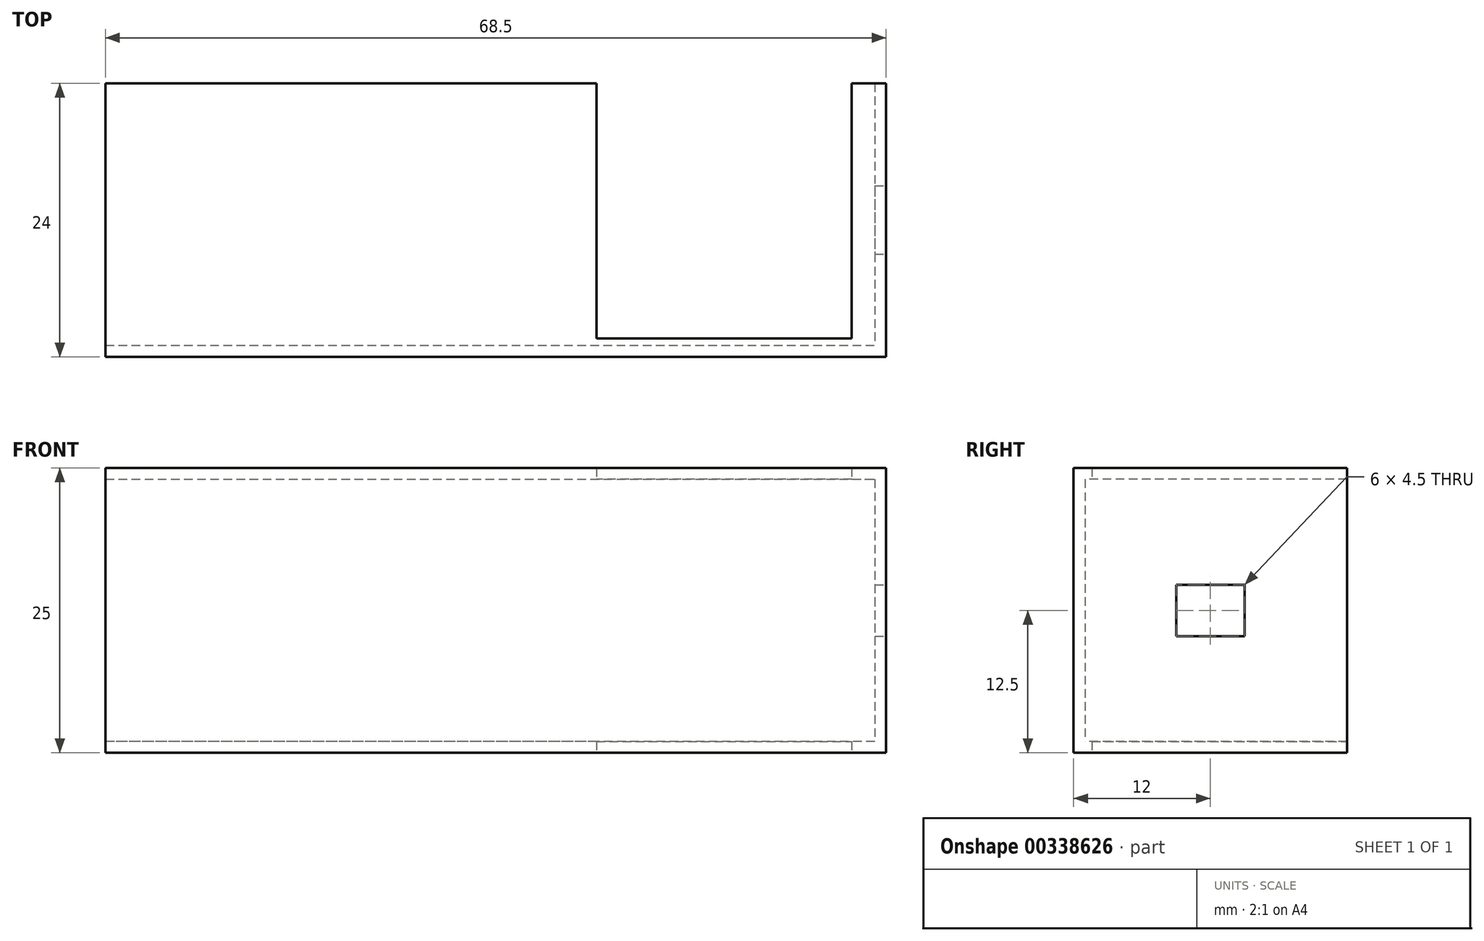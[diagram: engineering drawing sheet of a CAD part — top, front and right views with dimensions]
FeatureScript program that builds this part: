
annotation { "Feature Type Name" : "Feature", "Feature Type Description" : "" }
export const myFeature = defineFeature(function(context is Context, id is Id, definition is map)
    precondition{}
    {
        {
            var Q0;
            Q0=qCreatedBy(makeId("Front.planeOp"),FACE);
            var sketch = newSketch(context, id + "F0", { "sketchPlane" : qUnion([Q0])});
            skLineSegment(sketch, "E0.bottom", {"start": v(-34.25, 12.5) * mm, "end": v(34.25, 12.5) * mm});
            skLineSegment(sketch, "E0.top", {"start": v(-34.25, -12.5) * mm, "end": v(34.25, -12.5) * mm});
            skLineSegment(sketch, "E0.left", {"start": v(-34.25, 12.5) * mm, "end": v(-34.25, -12.5) * mm});
            skLineSegment(sketch, "E0.right", {"start": v(34.25, 12.5) * mm, "end": v(34.25, -12.5) * mm});
            skPoint(sketch, "E0.middle", {"position": v(0, 0) * mm});
            skSolve(sketch);
        }
        {
            var Q0;
            Q0 = qSketchRegion(id + "F0", true);
            extrude(context, id + "F1", {"entities" : qUnion([Q0]), "depth" : 1 * mm, "offsetDistance" : 25 * mm});
        }
        {
            var Q0;
            Q0=makeQuery(id+"F1.opExtrude","CAP_FACE",FACE,{"disambiguationData":[OSD([sQuery(id+"F0.wireOp",EDGE,"E0.bottom"),sQuery(id+"F0.wireOp",EDGE,"E0.top"),sQuery(id+"F0.wireOp",EDGE,"E0.left"),sQuery(id+"F0.wireOp",EDGE,"E0.right")])],"isStart":true});
            var sketch = newSketch(context, id + "F2", { "sketchPlane" : qUnion([Q0])});
            skLineSegment(sketch, "E1.bottom", {"start": v(-34.25, -12.5) * mm, "end": v(34.25, -12.5) * mm});
            skLineSegment(sketch, "E1.top", {"start": v(-34.25, -11.5) * mm, "end": v(34.25, -11.5) * mm});
            skLineSegment(sketch, "E1.left", {"start": v(-34.25, -12.5) * mm, "end": v(-34.25, -11.5) * mm});
            skLineSegment(sketch, "E1.right", {"start": v(34.25, -12.5) * mm, "end": v(34.25, -11.5) * mm});
            skSolve(sketch);
        }
        {
            var Q0;
            Q0 = qSketchRegion(id + "F2", true);
            extrude(context, id + "F3", {"entities" : qUnion([Q0]), "operationType" : NewBodyOperationType.ADD, "depth" : 23 * mm, "offsetDistance" : 25 * mm});
        }
        {
            var Q0;
            Q0=makeQuery(id+"F1.opExtrude","CAP_FACE",FACE,{"disambiguationData":[OSD([sQuery(id+"F0.wireOp",EDGE,"E0.bottom"),sQuery(id+"F0.wireOp",EDGE,"E0.top"),sQuery(id+"F0.wireOp",EDGE,"E0.left"),sQuery(id+"F0.wireOp",EDGE,"E0.right")])],"isStart":true});
            var sketch = newSketch(context, id + "F4", { "sketchPlane" : qUnion([Q0])});
            skLineSegment(sketch, "E2.bottom", {"start": v(-34.25, 12.5) * mm, "end": v(-33.25, 12.5) * mm});
            skLineSegment(sketch, "E2.top", {"start": v(-34.25, -11.5) * mm, "end": v(-33.25, -11.5) * mm});
            skLineSegment(sketch, "E2.left", {"start": v(-34.25, 12.5) * mm, "end": v(-34.25, -11.5) * mm});
            skLineSegment(sketch, "E2.right", {"start": v(-33.25, 12.5) * mm, "end": v(-33.25, -11.5) * mm});
            skSolve(sketch);
        }
        {
            var Q0;
            Q0 = qSketchRegion(id + "F4", true);
            extrude(context, id + "F5", {"entities" : qUnion([Q0]), "operationType" : NewBodyOperationType.ADD, "depth" : 23 * mm, "offsetDistance" : 25 * mm});
        }
        {
            var Q0;
            Q0=makeQuery(id+"F1.opExtrude","CAP_FACE",FACE,{"disambiguationData":[OSD([sQuery(id+"F0.wireOp",EDGE,"E0.bottom"),sQuery(id+"F0.wireOp",EDGE,"E0.top"),sQuery(id+"F0.wireOp",EDGE,"E0.left"),sQuery(id+"F0.wireOp",EDGE,"E0.right")])],"isStart":true});
            var sketch = newSketch(context, id + "F6", { "sketchPlane" : qUnion([Q0])});
            skLineSegment(sketch, "E3.bottom", {"start": v(34.25, 12.5) * mm, "end": v(-33.25, 12.5) * mm});
            skLineSegment(sketch, "E3.top", {"start": v(34.25, 11.5) * mm, "end": v(-33.25, 11.5) * mm});
            skLineSegment(sketch, "E3.left", {"start": v(34.25, 12.5) * mm, "end": v(34.25, 11.5) * mm});
            skLineSegment(sketch, "E3.right", {"start": v(-33.25, 12.5) * mm, "end": v(-33.25, 11.5) * mm});
            skSolve(sketch);
        }
        {
            var Q0;
            Q0 = qSketchRegion(id + "F6", true);
            extrude(context, id + "F7", {"entities" : qUnion([Q0]), "operationType" : NewBodyOperationType.ADD, "depth" : 23 * mm, "offsetDistance" : 25 * mm});
        }
        {
            var Q0;
            Q0=makeQuery(id+"F5.boolean.opBoolean","MERGE",FACE,{"derivedFrom":[makeQuery(id+"F3.boolean.opBoolean","MERGE",FACE,{"derivedFrom":[makeQuery(id+"F1.opExtrude","SWEPT_FACE",FACE,{"disambiguationData":[OSD([sQuery(id+"F0.wireOp",EDGE,"E0.right")])]}),makeQuery(id+"F3.opExtrude","SWEPT_FACE",FACE,{"disambiguationData":[OSD([sQuery(id+"F2.wireOp",EDGE,"E1.left")])]})]}),makeQuery(id+"F5.opExtrude","SWEPT_FACE",FACE,{"disambiguationData":[OSD([sQuery(id+"F4.wireOp",EDGE,"E2.left")])]})]});
            var sketch = newSketch(context, id + "F8", { "sketchPlane" : qUnion([Q0])});
            skLineSegment(sketch, "E4.bottom", {"start": v(14, 2.25) * mm, "end": v(8, 2.25) * mm});
            skLineSegment(sketch, "E4.top", {"start": v(14, -2.25) * mm, "end": v(8, -2.25) * mm});
            skLineSegment(sketch, "E4.left", {"start": v(14, 2.25) * mm, "end": v(14, -2.25) * mm});
            skLineSegment(sketch, "E4.right", {"start": v(8, 2.25) * mm, "end": v(8, -2.25) * mm});
            skPoint(sketch, "E4.middle", {"position": v(11, 0) * mm});
            skPoint(sketch, "E4.middle.positionSnap0", {"position": v(11, -12.5) * mm});
            skPoint(sketch, "E4.centerSnap0", {"position": v(11, -12.5) * mm});
            skSolve(sketch);
        }
        {
            var Q0;
            Q0=makeQuery(id+"F8.imprint","IMPRINT",FACE,{"disambiguationData":[TD([[makeQuery(id+"F8.imprint","IMPRINT",EDGE,{"derivedFrom":sQuery(id+"F8.wireOp",EDGE,"E4.bottom")}),1.0]])]});
            var Q1;
            Q1=makeQuery(id+"F5.opExtrude","SWEPT_FACE",FACE,{"disambiguationData":[OSD([sQuery(id+"F4.wireOp",EDGE,"E2.right")])]});
            extrude(context, id + "F9", {"entities" : qUnion([Q0]), "operationType" : NewBodyOperationType.REMOVE, "endBound" : BoundingType.UP_TO_SURFACE, "oppositeDirection" : true, "depth" : 25 * mm, "endBoundEntityFace" : qUnion([Q1]), "offsetDistance" : 25 * mm});
        }
        {
            var Q0;
            Q0=makeQuery(id+"F3.boolean.opBoolean","MERGE",FACE,{"derivedFrom":[makeQuery(id+"F1.opExtrude","SWEPT_FACE",FACE,{"disambiguationData":[OSD([sQuery(id+"F0.wireOp",EDGE,"E0.top")])]}),makeQuery(id+"F3.opExtrude","SWEPT_FACE",FACE,{"disambiguationData":[OSD([sQuery(id+"F2.wireOp",EDGE,"E1.bottom")])]})]});
            var sketch = newSketch(context, id + "F10", { "sketchPlane" : qUnion([Q0])});
            skPoint(sketch, "E5.centerSnap0", {"position": v(34.25, -11) * mm});
            skLineSegment(sketch, "E6.bottom", {"start": v(31.23, -23) * mm, "end": v(8.82, -23) * mm});
            skLineSegment(sketch, "E6.top", {"start": v(31.23, -0.62) * mm, "end": v(8.82, -0.62) * mm});
            skLineSegment(sketch, "E6.left", {"start": v(31.23, -23) * mm, "end": v(31.23, -0.62) * mm});
            skLineSegment(sketch, "E6.right", {"start": v(8.82, -23) * mm, "end": v(8.82, -0.62) * mm});
            skSolve(sketch);
        }
        {
            var Q0;
            Q0 = qSketchRegion(id + "F10", true);
            var Q1;
            Q1=makeQuery(id+"F3.opExtrude","SWEPT_FACE",FACE,{"disambiguationData":[OSD([sQuery(id+"F2.wireOp",EDGE,"E1.top")])]});
            extrude(context, id + "F11", {"entities" : qUnion([Q0]), "operationType" : NewBodyOperationType.REMOVE, "oppositeDirection" : true, "depth" : 25 * mm, "endBoundEntityFace" : qUnion([Q1]), "offsetDistance" : 25 * mm});
        }
    });
